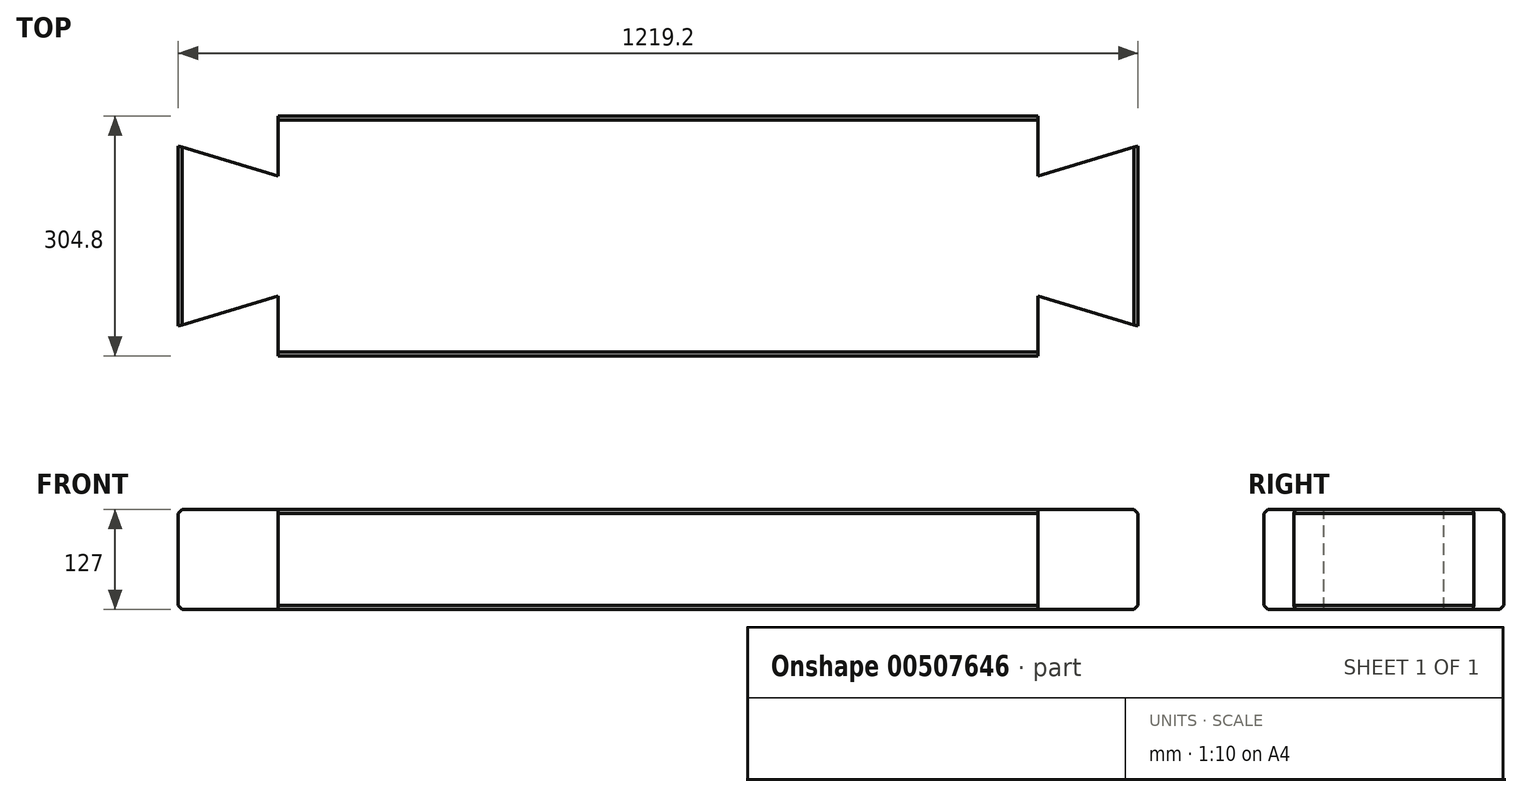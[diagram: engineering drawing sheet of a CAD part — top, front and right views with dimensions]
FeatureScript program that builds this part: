
annotation { "Feature Type Name" : "Feature", "Feature Type Description" : "" }
export const myFeature = defineFeature(function(context is Context, id is Id, definition is map)
    precondition{}
    {
        {
            var Q0;
            Q0=qCreatedBy(makeId("Top.planeOp"),FACE);
            var sketch = newSketch(context, id + "F0", { "sketchPlane" : qUnion([Q0])});
            skLineSegment(sketch, "E0.bottom", {"start": v(-609.6, 152.4) * mm, "end": v(609.6, 152.4) * mm});
            skLineSegment(sketch, "E0.top", {"start": v(-609.6, -152.4) * mm, "end": v(609.6, -152.4) * mm});
            skLineSegment(sketch, "E0.left", {"start": v(-609.6, 152.4) * mm, "end": v(-609.6, -152.4) * mm});
            skLineSegment(sketch, "E0.right", {"start": v(609.6, 152.4) * mm, "end": v(609.6, -152.4) * mm});
            skSolve(sketch);
        }
        {
            var Q0;
            Q0 = qSketchRegion(id + "F0", true);
            extrude(context, id + "F1", {"entities" : qUnion([Q0]), "depth" : 63.5 * mm, "hasSecondDirection" : true, "secondDirectionOppositeDirection" : true, "secondDirectionDepth" : 63.5 * mm});
        }
        {
            var Q0;
            Q0=makeQuery(id+"F1.opExtrude","CAP_FACE",FACE,{"disambiguationData":[OSD([sQuery(id+"F0.wireOp",EDGE,"E0.bottom"),sQuery(id+"F0.wireOp",EDGE,"E0.top"),sQuery(id+"F0.wireOp",EDGE,"E0.left"),sQuery(id+"F0.wireOp",EDGE,"E0.right")])],"isStart":false});
            var sketch = newSketch(context, id + "F2", { "sketchPlane" : qUnion([Q0])});
            skLineSegment(sketch, "E1", {"start": v(-609.6, 152.4) * mm, "end": v(-482.6, 152.4) * mm});
            skLineSegment(sketch, "E2", {"start": v(-482.6, 152.4) * mm, "end": v(-482.6, 76.2) * mm});
            skLineSegment(sketch, "E3", {"start": v(-482.6, 76.2) * mm, "end": v(-609.6, 114.3) * mm});
            skLineSegment(sketch, "E4", {"start": v(-609.6, 114.3) * mm, "end": v(-609.6, 152.4) * mm});
            skLineSegment(sketch, "E5.MirrorCS", {"start": v(-482.6, -76.2) * mm, "end": v(-609.6, -114.3) * mm});
            skLineSegment(sketch, "E6.MirrorCS", {"start": v(-482.6, -152.4) * mm, "end": v(-482.6, -76.2) * mm});
            skLineSegment(sketch, "E7.MirrorCS", {"start": v(-609.6, -152.4) * mm, "end": v(-482.6, -152.4) * mm});
            skLineSegment(sketch, "E8.MirrorCS", {"start": v(-609.6, -114.3) * mm, "end": v(-609.6, -152.4) * mm});
            skLineSegment(sketch, "E9.MirrorCS", {"start": v(482.6, 152.4) * mm, "end": v(482.6, 76.2) * mm});
            skLineSegment(sketch, "E10.MirrorCS", {"start": v(609.6, 152.4) * mm, "end": v(482.6, 152.4) * mm});
            skLineSegment(sketch, "E11.MirrorCS", {"start": v(609.6, 114.3) * mm, "end": v(609.6, 152.4) * mm});
            skLineSegment(sketch, "E12.MirrorCS", {"start": v(482.6, 76.2) * mm, "end": v(609.6, 114.3) * mm});
            skLineSegment(sketch, "E13.MirrorCS", {"start": v(482.6, -76.2) * mm, "end": v(609.6, -114.3) * mm});
            skLineSegment(sketch, "E14.MirrorCS", {"start": v(482.6, -152.4) * mm, "end": v(482.6, -76.2) * mm});
            skLineSegment(sketch, "E15.MirrorCS", {"start": v(609.6, -152.4) * mm, "end": v(482.6, -152.4) * mm});
            skLineSegment(sketch, "E16.MirrorCS", {"start": v(609.6, -114.3) * mm, "end": v(609.6, -152.4) * mm});
            skSolve(sketch);
        }
        {
            var Q0;
            Q0 = qSketchRegion(id + "F2", true);
            extrude(context, id + "F3", {"entities" : qUnion([Q0]), "operationType" : NewBodyOperationType.REMOVE, "endBound" : BoundingType.UP_TO_NEXT, "oppositeDirection" : true, "depth" : 25.4 * mm});
        }
        {
            var Q0;
            Q0=makeQuery(id+"F3.boolean.opBoolean","COPY",EDGE,{"derivedFrom":makeQuery(id+"F3.opExtrude","CAP_EDGE",EDGE,{"disambiguationData":[OSD([sQuery(id+"F2.wireOp",EDGE,"E5.MirrorCS")])],"isStart":true})});
            var Q1;
            Q1=makeQuery(id+"F1.opExtrude","CAP_EDGE",EDGE,{"disambiguationData":[OSD([sQuery(id+"F0.wireOp",EDGE,"E0.left")])],"isStart":false});
            var Q2;
            Q2=makeQuery(id+"F3.boolean.opBoolean","COPY",EDGE,{"derivedFrom":makeQuery(id+"F3.opExtrude","CAP_EDGE",EDGE,{"disambiguationData":[OSD([sQuery(id+"F2.wireOp",EDGE,"E3")])],"isStart":true})});
            var Q3;
            Q3=makeQuery(id+"F3.boolean.opBoolean","COPY",EDGE,{"derivedFrom":makeQuery(id+"F3.opExtrude","CAP_EDGE",EDGE,{"disambiguationData":[OSD([sQuery(id+"F2.wireOp",EDGE,"E2")])],"isStart":true})});
            var Q4;
            Q4=makeQuery(id+"F1.opExtrude","CAP_EDGE",EDGE,{"disambiguationData":[OSD([sQuery(id+"F0.wireOp",EDGE,"E0.bottom")])],"isStart":false});
            var Q5;
            Q5=makeQuery(id+"F3.boolean.opBoolean","COPY",EDGE,{"derivedFrom":makeQuery(id+"F3.opExtrude","CAP_EDGE",EDGE,{"disambiguationData":[OSD([sQuery(id+"F2.wireOp",EDGE,"E9.MirrorCS")])],"isStart":true})});
            var Q6;
            Q6=makeQuery(id+"F3.boolean.opBoolean","COPY",EDGE,{"derivedFrom":makeQuery(id+"F3.opExtrude","CAP_EDGE",EDGE,{"disambiguationData":[OSD([sQuery(id+"F2.wireOp",EDGE,"E12.MirrorCS")])],"isStart":true})});
            var Q7;
            Q7=makeQuery(id+"F1.opExtrude","CAP_EDGE",EDGE,{"disambiguationData":[OSD([sQuery(id+"F0.wireOp",EDGE,"E0.right")])],"isStart":false});
            var Q8;
            Q8=makeQuery(id+"F3.boolean.opBoolean","COPY",EDGE,{"derivedFrom":makeQuery(id+"F3.opExtrude","CAP_EDGE",EDGE,{"disambiguationData":[OSD([sQuery(id+"F2.wireOp",EDGE,"E13.MirrorCS")])],"isStart":true})});
            var Q9;
            Q9=makeQuery(id+"F3.boolean.opBoolean","COPY",EDGE,{"derivedFrom":makeQuery(id+"F3.opExtrude","CAP_EDGE",EDGE,{"disambiguationData":[OSD([sQuery(id+"F2.wireOp",EDGE,"E14.MirrorCS")])],"isStart":true})});
            var Q10;
            Q10=makeQuery(id+"F1.opExtrude","CAP_EDGE",EDGE,{"disambiguationData":[OSD([sQuery(id+"F0.wireOp",EDGE,"E0.top")])],"isStart":false});
            var Q11;
            Q11=makeQuery(id+"F3.boolean.opBoolean","COPY",EDGE,{"derivedFrom":makeQuery(id+"F3.opExtrude","CAP_EDGE",EDGE,{"disambiguationData":[OSD([sQuery(id+"F2.wireOp",EDGE,"E6.MirrorCS")])],"isStart":true})});
            var Q12;
            Q12=makeQuery(id+"F1.opExtrude","CAP_EDGE",EDGE,{"disambiguationData":[OSD([sQuery(id+"F0.wireOp",EDGE,"E0.left")])],"isStart":true});
            var Q13;
            Q13=makeQuery(id+"F3.boolean.opBoolean","COPY",EDGE,{"derivedFrom":makeQuery(id+"F3.opExtrude","CAP_EDGE",EDGE,{"disambiguationData":[OSD([sQuery(id+"F2.wireOp",EDGE,"E3")])],"isStart":false})});
            var Q14;
            Q14=makeQuery(id+"F3.boolean.opBoolean","COPY",EDGE,{"derivedFrom":makeQuery(id+"F3.opExtrude","CAP_EDGE",EDGE,{"disambiguationData":[OSD([sQuery(id+"F2.wireOp",EDGE,"E2")])],"isStart":false})});
            var Q15;
            Q15=makeQuery(id+"F1.opExtrude","CAP_EDGE",EDGE,{"disambiguationData":[OSD([sQuery(id+"F0.wireOp",EDGE,"E0.bottom")])],"isStart":true});
            var Q16;
            Q16=makeQuery(id+"F3.boolean.opBoolean","COPY",EDGE,{"derivedFrom":makeQuery(id+"F3.opExtrude","CAP_EDGE",EDGE,{"disambiguationData":[OSD([sQuery(id+"F2.wireOp",EDGE,"E9.MirrorCS")])],"isStart":false})});
            var Q17;
            Q17=makeQuery(id+"F3.boolean.opBoolean","COPY",EDGE,{"derivedFrom":makeQuery(id+"F3.opExtrude","CAP_EDGE",EDGE,{"disambiguationData":[OSD([sQuery(id+"F2.wireOp",EDGE,"E12.MirrorCS")])],"isStart":false})});
            var Q18;
            Q18=makeQuery(id+"F1.opExtrude","CAP_EDGE",EDGE,{"disambiguationData":[OSD([sQuery(id+"F0.wireOp",EDGE,"E0.right")])],"isStart":true});
            var Q19;
            Q19=makeQuery(id+"F3.boolean.opBoolean","COPY",EDGE,{"derivedFrom":makeQuery(id+"F3.opExtrude","CAP_EDGE",EDGE,{"disambiguationData":[OSD([sQuery(id+"F2.wireOp",EDGE,"E13.MirrorCS")])],"isStart":false})});
            var Q20;
            Q20=makeQuery(id+"F3.boolean.opBoolean","COPY",EDGE,{"derivedFrom":makeQuery(id+"F3.opExtrude","CAP_EDGE",EDGE,{"disambiguationData":[OSD([sQuery(id+"F2.wireOp",EDGE,"E14.MirrorCS")])],"isStart":false})});
            var Q21;
            Q21=makeQuery(id+"F1.opExtrude","CAP_EDGE",EDGE,{"disambiguationData":[OSD([sQuery(id+"F0.wireOp",EDGE,"E0.top")])],"isStart":true});
            var Q22;
            Q22=makeQuery(id+"F3.boolean.opBoolean","COPY",EDGE,{"derivedFrom":makeQuery(id+"F3.opExtrude","CAP_EDGE",EDGE,{"disambiguationData":[OSD([sQuery(id+"F2.wireOp",EDGE,"E6.MirrorCS")])],"isStart":false})});
            var Q23;
            Q23=makeQuery(id+"F3.boolean.opBoolean","COPY",EDGE,{"derivedFrom":makeQuery(id+"F3.opExtrude","CAP_EDGE",EDGE,{"disambiguationData":[OSD([sQuery(id+"F2.wireOp",EDGE,"E5.MirrorCS")])],"isStart":false})});
            var Q24;
            Q24=makeQuery(id+"F3.boolean.opBoolean","COPY",EDGE,{"derivedFrom":makeQuery(id+"F3.opExtrude","SWEPT_EDGE",EDGE,{"disambiguationData":[OSD([sQuery(id+"F0.wireOp",EDGE,"E0.top"),sQuery(id+"F2.wireOp",EDGE,"E6.MirrorCS"),sQuery(id+"F2.wireOp",EDGE,"E7.MirrorCS")])]})});
            var Q25;
            Q25=makeQuery(id+"F3.boolean.opBoolean","COPY",EDGE,{"derivedFrom":makeQuery(id+"F3.opExtrude","SWEPT_EDGE",EDGE,{"disambiguationData":[OSD([sQuery(id+"F0.wireOp",EDGE,"E0.left"),sQuery(id+"F2.wireOp",EDGE,"E5.MirrorCS"),sQuery(id+"F2.wireOp",EDGE,"E8.MirrorCS")])]})});
            var Q26;
            Q26=makeQuery(id+"F3.boolean.opBoolean","COPY",EDGE,{"derivedFrom":makeQuery(id+"F3.opExtrude","SWEPT_EDGE",EDGE,{"disambiguationData":[OSD([sQuery(id+"F0.wireOp",EDGE,"E0.left"),sQuery(id+"F2.wireOp",EDGE,"E3"),sQuery(id+"F2.wireOp",EDGE,"E4")])]})});
            var Q27;
            Q27=makeQuery(id+"F3.boolean.opBoolean","COPY",EDGE,{"derivedFrom":makeQuery(id+"F3.opExtrude","SWEPT_EDGE",EDGE,{"disambiguationData":[OSD([sQuery(id+"F0.wireOp",EDGE,"E0.bottom"),sQuery(id+"F2.wireOp",EDGE,"E1"),sQuery(id+"F2.wireOp",EDGE,"E2")])]})});
            var Q28;
            Q28=makeQuery(id+"F3.boolean.opBoolean","COPY",EDGE,{"derivedFrom":makeQuery(id+"F3.opExtrude","SWEPT_EDGE",EDGE,{"disambiguationData":[OSD([sQuery(id+"F0.wireOp",EDGE,"E0.top"),sQuery(id+"F2.wireOp",EDGE,"E14.MirrorCS"),sQuery(id+"F2.wireOp",EDGE,"E15.MirrorCS")])]})});
            var Q29;
            Q29=makeQuery(id+"F3.boolean.opBoolean","COPY",EDGE,{"derivedFrom":makeQuery(id+"F3.opExtrude","SWEPT_EDGE",EDGE,{"disambiguationData":[OSD([sQuery(id+"F0.wireOp",EDGE,"E0.right"),sQuery(id+"F2.wireOp",EDGE,"E13.MirrorCS"),sQuery(id+"F2.wireOp",EDGE,"E16.MirrorCS")])]})});
            var Q30;
            Q30=makeQuery(id+"F3.boolean.opBoolean","COPY",EDGE,{"derivedFrom":makeQuery(id+"F3.opExtrude","SWEPT_EDGE",EDGE,{"disambiguationData":[OSD([sQuery(id+"F0.wireOp",EDGE,"E0.right"),sQuery(id+"F2.wireOp",EDGE,"E11.MirrorCS"),sQuery(id+"F2.wireOp",EDGE,"E12.MirrorCS")])]})});
            var Q31;
            Q31=makeQuery(id+"F3.boolean.opBoolean","COPY",EDGE,{"derivedFrom":makeQuery(id+"F3.opExtrude","SWEPT_EDGE",EDGE,{"disambiguationData":[OSD([sQuery(id+"F0.wireOp",EDGE,"E0.bottom"),sQuery(id+"F2.wireOp",EDGE,"E9.MirrorCS"),sQuery(id+"F2.wireOp",EDGE,"E10.MirrorCS")])]})});
            chamfer(context, id + "F4", {"entities" : qUnion([Q0, Q1, Q2, Q3, Q4, Q5, Q6, Q7, Q8, Q9, Q10, Q11, Q12, Q13, Q14, Q15, Q16, Q17, Q18, Q19, Q20, Q21, Q22, Q23, Q24, Q25, Q26, Q27, Q28, Q29, Q30, Q31]), "width" : 5.08 * mm, "tangentPropagation" : true});
        }
    });
